# Revit family: FP-Revit19-FM2060S1-Plinth-90002791A
name_source: partatom
category: Specialty Equipment
units: mm (PartAtom-declared; Revit-internal decimal feet)

## family parameters
Always vertical = Yes
Cut with Voids When Loaded = Yes
Part Type = Normal
Room Calculation Point = No
Round Connector Dimension = Use Diameter
Shared = No
Work Plane-Based = No

## types (2) — shared parameters
Cavity - Depth = 655 mm  [stored 2.14895 ft]
Cavity - Height (195mm - 205mm) = 200 mm  [stored 0.656168 ft]
Cavity - Width = 624 mm  [stored 2.04724 ft]
Chassis - Depth = 545 mm  [stored 1.78806 ft]
Chassis - Height = 159 mm  [stored 0.521654 ft]
Chassis - Width = 600 mm
Manufacturer = Fisher & Paykel Appliances Ltd
Material - Body = Fisher & Paykel - Grey
Product - Depth = 605 mm  [stored 1.98491 ft]
Product - Height (192mm - 202mm) = 197 mm
Product - Width = 600 mm
Visibility - Clearance Required = Yes
zero-valued in all types: Default Elevation

## per-type parameters (varying)
| type | Material - Front |
| FM2060S1 | Fisher & Paykel - White |
| FM2060SG1 | Fisher & Paykel - Grey, Charcoal |

note: column(s) folded — value = type name in every type: Model

note: [stored X ft] marks values corroborated as IEEE doubles in the binary element streams (Revit-internal decimal feet)

## geometry (parser evidence)
native form markers: Sweep x2
no freeform markers — native parametric forms only
